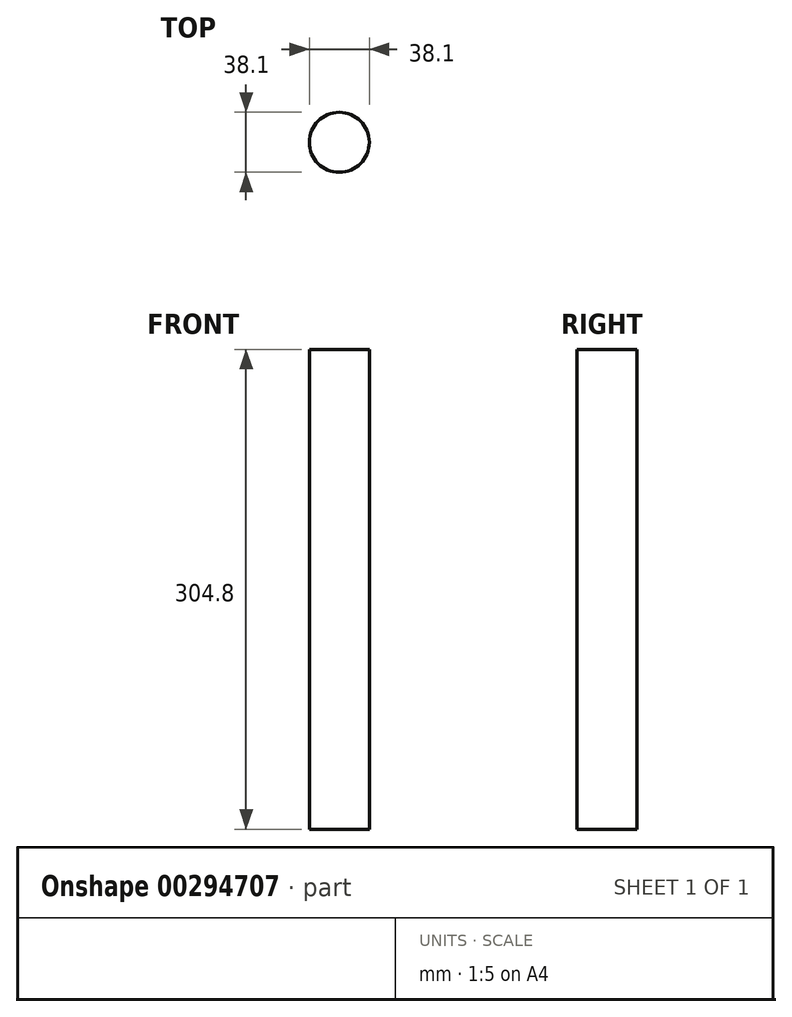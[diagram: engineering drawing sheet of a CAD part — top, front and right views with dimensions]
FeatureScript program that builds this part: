
annotation { "Feature Type Name" : "Feature", "Feature Type Description" : "" }
export const myFeature = defineFeature(function(context is Context, id is Id, definition is map)
    precondition{}
    {
        {
            var Q0;
            Q0=qCreatedBy(makeId("Top.planeOp"),FACE);
            var sketch = newSketch(context, id + "F0", { "sketchPlane" : qUnion([Q0])});
            skCircle(sketch, "E0", {"center": v(0, 0) * mm, "radius": 19.05 * mm});
            skSolve(sketch);
        }
        {
            var Q0;
            Q0 = qSketchRegion(id + "F0", true);
            extrude(context, id + "F1", {"entities" : qUnion([Q0]), "depth" : 304.8 * mm});
        }
    });
